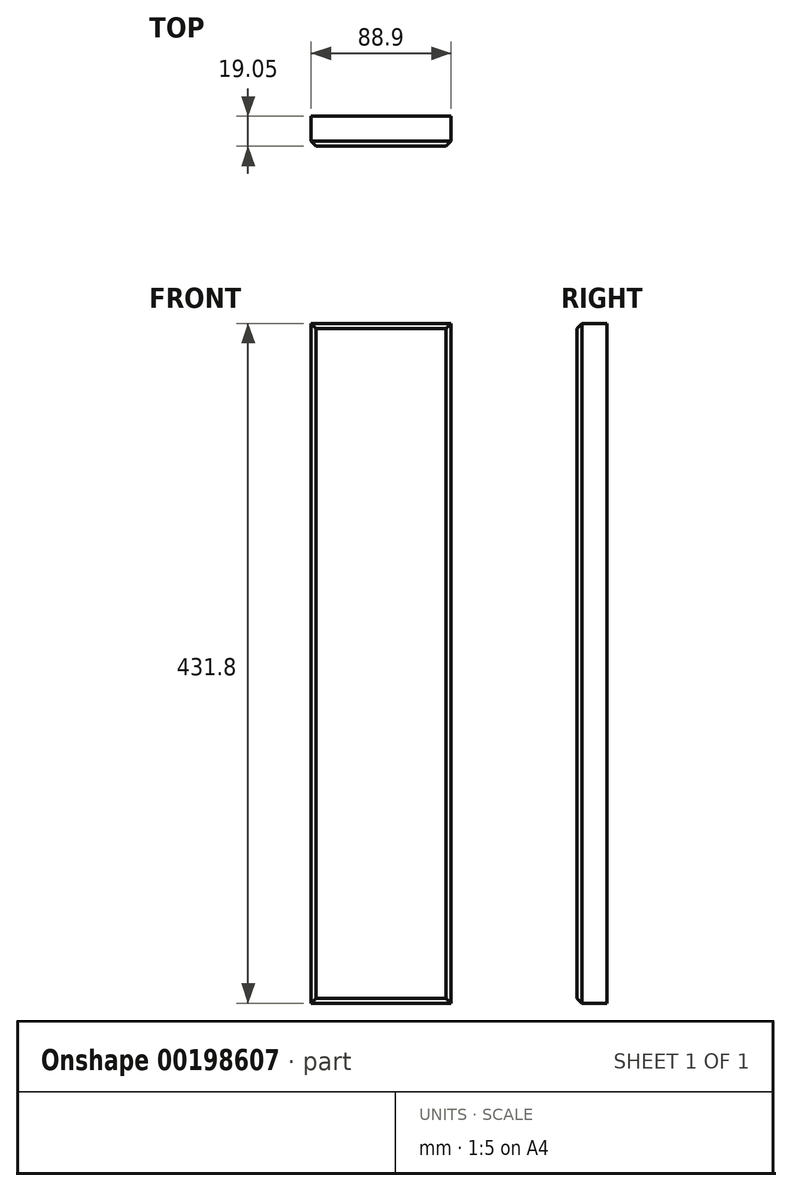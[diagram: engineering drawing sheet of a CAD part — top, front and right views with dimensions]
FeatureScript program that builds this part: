
annotation { "Feature Type Name" : "Feature", "Feature Type Description" : "" }
export const myFeature = defineFeature(function(context is Context, id is Id, definition is map)
    precondition{}
    {
        {
            var Q0;
            Q0=qCreatedBy(makeId("Top.planeOp"),FACE);
            var sketch = newSketch(context, id + "F0", { "sketchPlane" : qUnion([Q0])});
            skLineSegment(sketch, "E0.bottom", {"start": v(0, 0) * mm, "end": v(88.9, 0) * mm});
            skLineSegment(sketch, "E0.top", {"start": v(0, 19.05) * mm, "end": v(88.9, 19.05) * mm});
            skLineSegment(sketch, "E0.left", {"start": v(0, 0) * mm, "end": v(0, 19.05) * mm});
            skLineSegment(sketch, "E0.right", {"start": v(88.9, 0) * mm, "end": v(88.9, 19.05) * mm});
            skSolve(sketch);
        }
        {
            var Q0;
            Q0 = qSketchRegion(id + "F0", true);
            extrude(context, id + "F1", {"entities" : qUnion([Q0]), "depth" : 431.8 * mm});
        }
        {
            var Q0;
            Q0=makeQuery(id+"F1.opExtrude","CAP_EDGE",EDGE,{"disambiguationData":[OSD([sQuery(id+"F0.wireOp",EDGE,"E0.bottom")])],"isStart":true});
            var Q1;
            Q1=makeQuery(id+"F1.opExtrude","SWEPT_EDGE",EDGE,{"disambiguationData":[OSD([sQuery(id+"F0.wireOp",EDGE,"E0.bottom"),sQuery(id+"F0.wireOp",EDGE,"E0.left")])]});
            var Q2;
            Q2=makeQuery(id+"F1.opExtrude","SWEPT_EDGE",EDGE,{"disambiguationData":[OSD([sQuery(id+"F0.wireOp",EDGE,"E0.bottom"),sQuery(id+"F0.wireOp",EDGE,"E0.right")])]});
            var Q3;
            Q3=makeQuery(id+"F1.opExtrude","CAP_EDGE",EDGE,{"disambiguationData":[OSD([sQuery(id+"F0.wireOp",EDGE,"E0.bottom")])],"isStart":false});
            chamfer(context, id + "F2", {"entities" : qUnion([Q0, Q1, Q2, Q3]), "width" : 3.17 * mm, "tangentPropagation" : true});
        }
    });
